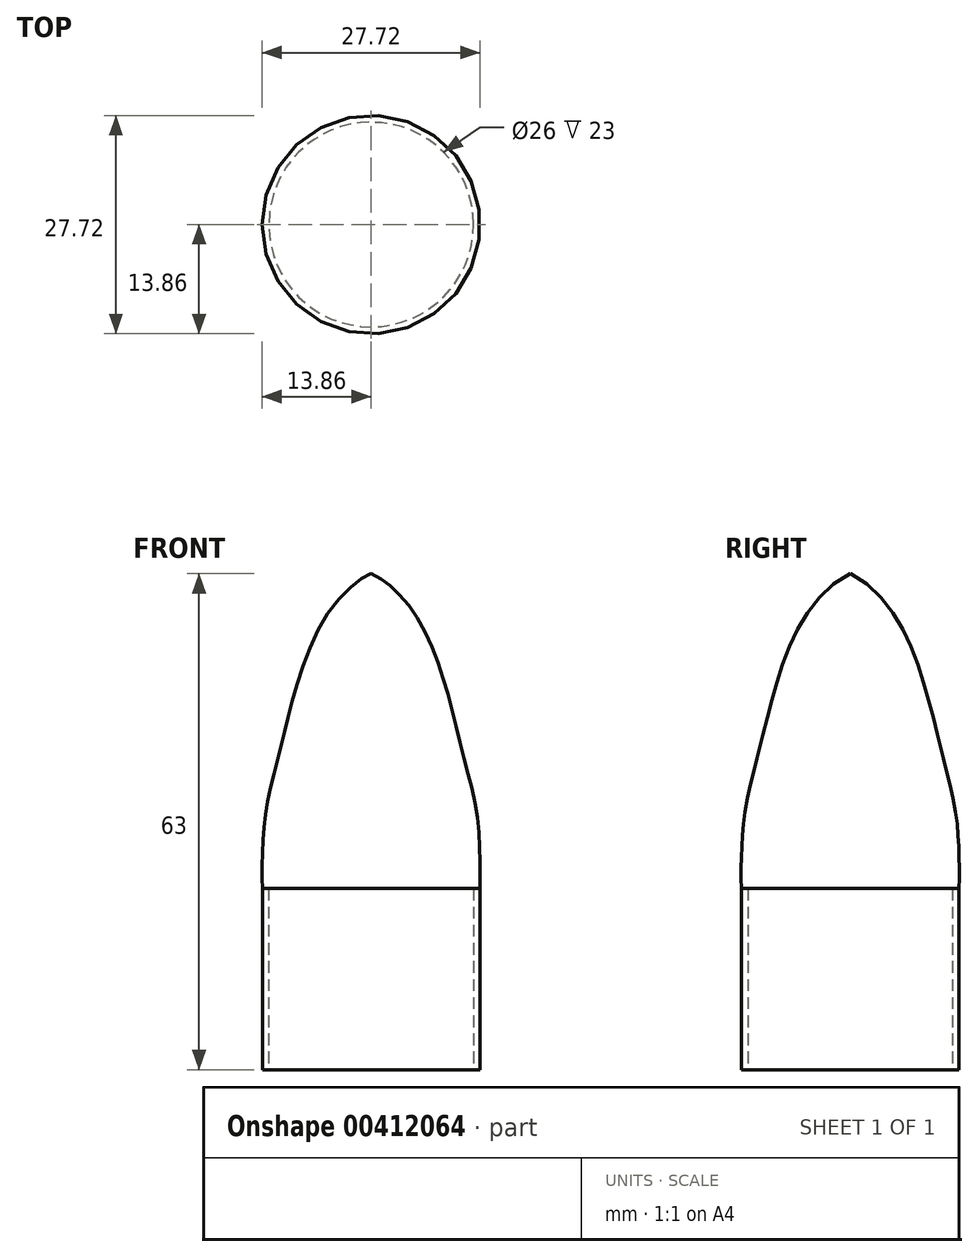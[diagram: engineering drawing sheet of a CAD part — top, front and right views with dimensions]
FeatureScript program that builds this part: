
annotation { "Feature Type Name" : "Feature", "Feature Type Description" : "" }
export const myFeature = defineFeature(function(context is Context, id is Id, definition is map)
    precondition{}
    {
        {
            var Q0;
            Q0=qCreatedBy(makeId("Front.planeOp"),FACE);
            var sketch = newSketch(context, id + "F0", { "sketchPlane" : qUnion([Q0])});
            skLineSegment(sketch, "E0", {"start": v(-13, 0) * mm, "end": v(-13, 23) * mm});
            skLineSegment(sketch, "E1", {"start": v(-13.8, 0) * mm, "end": v(-13.8, 23) * mm});
            skFitSpline(sketch, "E2", {"points": [v(-13.8, 23) * mm, v(-13.8, 27.71) * mm, v(-13.3, 33.26) * mm, v(-11.76, 39.76) * mm, v(-9.9, 47.19) * mm, v(-5.26, 58.33) * mm, v(0, 63) * mm], "startDerivative": vector(-2.22, 26.5) * mm, "endDerivative": vector(24.06, 8.68) * mm});
            skLineSegment(sketch, "E3", {"start": v(-13, 23) * mm, "end": v(0, 23) * mm});
            skLineSegment(sketch, "E4", {"start": v(0, 0) * mm, "end": v(0, 70.88) * mm});
            skLineSegment(sketch, "E5", {"start": v(-13, 0) * mm, "end": v(-13.8, 0) * mm});
            skSolve(sketch);
        }
        {
            var Q0;
            Q0=makeQuery(id+"F0.imprint","IMPRINT",FACE,{"disambiguationData":[TD([[makeQuery(id+"F0.imprint","IMPRINT",EDGE,{"derivedFrom":sQuery(id+"F0.wireOp",EDGE,"E0")}),1.0]])]});
            var Q1;
            Q1=sQuery(id+"F0.wireOp",EDGE,"E4");
            revolve(context, id + "F1", {"entities" : qUnion([Q0]), "axis" : qUnion([Q1]), "revolveType" : RevolveType.FULL});
        }
    });
